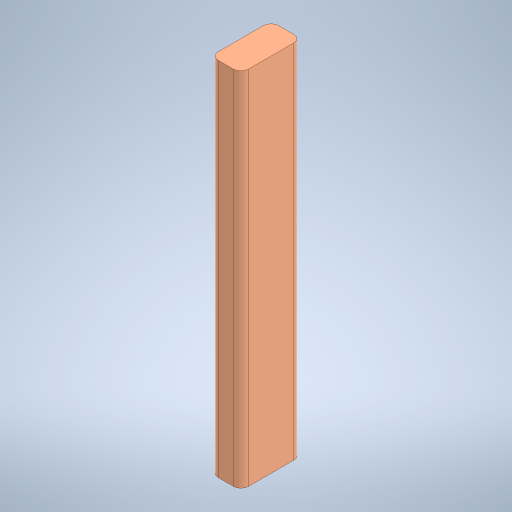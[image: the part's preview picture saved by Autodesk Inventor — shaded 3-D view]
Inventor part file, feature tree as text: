
AUTODESK INVENTOR PART (.ipt)
format: ipt  version: 2024 (Build 280153000, 153)  size: 242,688 bytes
history: native  units: mm
features: extrude x1
ambient origin geometry x8: Origin, YZ Plane, XZ Plane, XY Plane, X Axis, Y Axis, Z Axis, Center Point
bodies: Solid1 (feature_tree)
feature tree (1):
  extrude  "Extrusion1"  Depth=101.6mm
